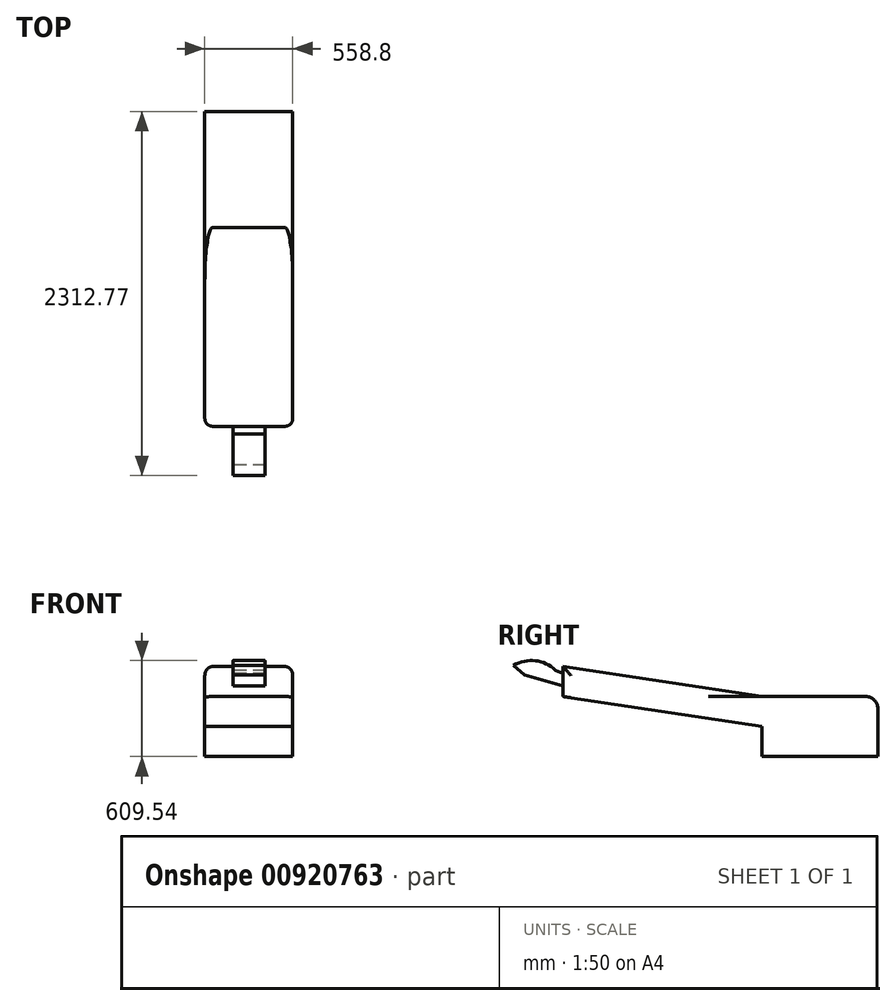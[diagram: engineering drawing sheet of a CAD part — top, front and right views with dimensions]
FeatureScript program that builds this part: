
annotation { "Feature Type Name" : "Feature", "Feature Type Description" : "" }
export const myFeature = defineFeature(function(context is Context, id is Id, definition is map)
    precondition{}
    {
        {
            var Q0;
            Q0=qCreatedBy(makeId("Top.planeOp"),FACE);
            var sketch = newSketch(context, id + "F0", { "sketchPlane" : qUnion([Q0])});
            skLineSegment(sketch, "E0.bottom", {"start": v(279.4, 368.3) * mm, "end": v(-279.4, 368.3) * mm});
            skLineSegment(sketch, "E0.top", {"start": v(279.4, -368.3) * mm, "end": v(-279.4, -368.3) * mm});
            skLineSegment(sketch, "E0.left", {"start": v(279.4, 368.3) * mm, "end": v(279.4, -368.3) * mm});
            skLineSegment(sketch, "E0.right", {"start": v(-279.4, 368.3) * mm, "end": v(-279.4, -368.3) * mm});
            skPoint(sketch, "E0.middle", {"position": v(0, 0) * mm});
            skSolve(sketch);
        }
        {
            var Q0;
            Q0 = qSketchRegion(id + "F0", true);
            extrude(context, id + "F1", {"entities" : qUnion([Q0]), "depth" : 381 * mm, "offsetDistance" : 25.4 * mm});
        }
        {
            var Q0;
            Q0=qCreatedBy(makeId("Right.planeOp"),FACE);
            var sketch = newSketch(context, id + "F2", { "sketchPlane" : qUnion([Q0])});
            skLineSegment(sketch, "E1", {"start": v(-368.3, 190.5) * mm, "end": v(-1631.65, 381) * mm});
            skLineSegment(sketch, "E2", {"start": v(-1631.65, 571.75) * mm, "end": v(-368.3, 381) * mm});
            skLineSegment(sketch, "E3", {"start": v(-368.3, 381) * mm, "end": v(-368.3, 190.5) * mm});
            skLineSegment(sketch, "E4", {"start": v(-1631.65, 381) * mm, "end": v(-1631.65, 571.75) * mm});
            skSolve(sketch);
        }
        {
            var Q0;
            Q0 = qSketchRegion(id + "F2", true);
            extrude(context, id + "F3", {"entities" : qUnion([Q0]), "operationType" : NewBodyOperationType.ADD, "endBound" : BoundingType.SYMMETRIC, "depth" : 558.8 * mm, "offsetDistance" : 25.4 * mm});
        }
        {
            var Q0;
            Q0=qCreatedBy(makeId("Right.planeOp"),FACE);
            var sketch = newSketch(context, id + "F4", { "sketchPlane" : qUnion([Q0])});
            skLineSegment(sketch, "E5", {"start": v(-1631.65, 449.14) * mm, "end": v(-1877.15, 518.44) * mm});
            skLineSegment(sketch, "E6", {"start": v(-1877.15, 518.44) * mm, "end": v(-1944.47, 577.83) * mm});
            skLineSegment(sketch, "E7", {"start": v(-1631.65, 449.14) * mm, "end": v(-1631.65, 526.36) * mm});
            skLineSegment(sketch, "E8", {"start": v(-1631.65, 526.36) * mm, "end": v(-1679.17, 548.14) * mm});
            skArc(sketch, "E9", {"start": v(-1679.17, 548.14) * mm, "mid": v(-1806.76, 608.18) * mm, "end": v(-1944.47, 577.83) * mm});
            skSolve(sketch);
        }
        {
            var Q0;
            Q0 = qSketchRegion(id + "F4", true);
            extrude(context, id + "F5", {"entities" : qUnion([Q0]), "operationType" : NewBodyOperationType.ADD, "endBound" : BoundingType.SYMMETRIC, "depth" : 203.2 * mm, "offsetDistance" : 25.4 * mm});
        }
        {
            var Q0;
            Q0=makeQuery(id+"F3.opExtrude","CAP_EDGE",EDGE,{"disambiguationData":[OSD([sQuery(id+"F2.wireOp",EDGE,"E2")])],"isStart":false});
            var Q1;
            Q1=makeQuery(id+"F3.opExtrude","CAP_EDGE",EDGE,{"disambiguationData":[OSD([sQuery(id+"F2.wireOp",EDGE,"E2")])],"isStart":true});
            var Q2;
            Q2=makeQuery(id+"F3.opExtrude","CAP_EDGE",EDGE,{"disambiguationData":[OSD([sQuery(id+"F2.wireOp",EDGE,"E4")])],"isStart":true});
            var Q3;
            Q3=makeQuery(id+"F3.opExtrude","CAP_EDGE",EDGE,{"disambiguationData":[OSD([sQuery(id+"F2.wireOp",EDGE,"E4")])],"isStart":false});
            fillet(context, id + "F6", {"entities" : qUnion([Q0, Q1, Q2, Q3]), "radius" : 50.8 * mm, "tangentPropagation" : true, "allowEdgeOverflow" : false});
        }
        {
            var Q0;
            Q0=makeQuery(id+"F1.opExtrude","CAP_EDGE",EDGE,{"disambiguationData":[OSD([sQuery(id+"F0.wireOp",EDGE,"E0.bottom")])],"isStart":false});
            fillet(context, id + "F7", {"entities" : qUnion([Q0]), "radius" : 76.2 * mm, "tangentPropagation" : true, "allowEdgeOverflow" : false});
        }
    });
